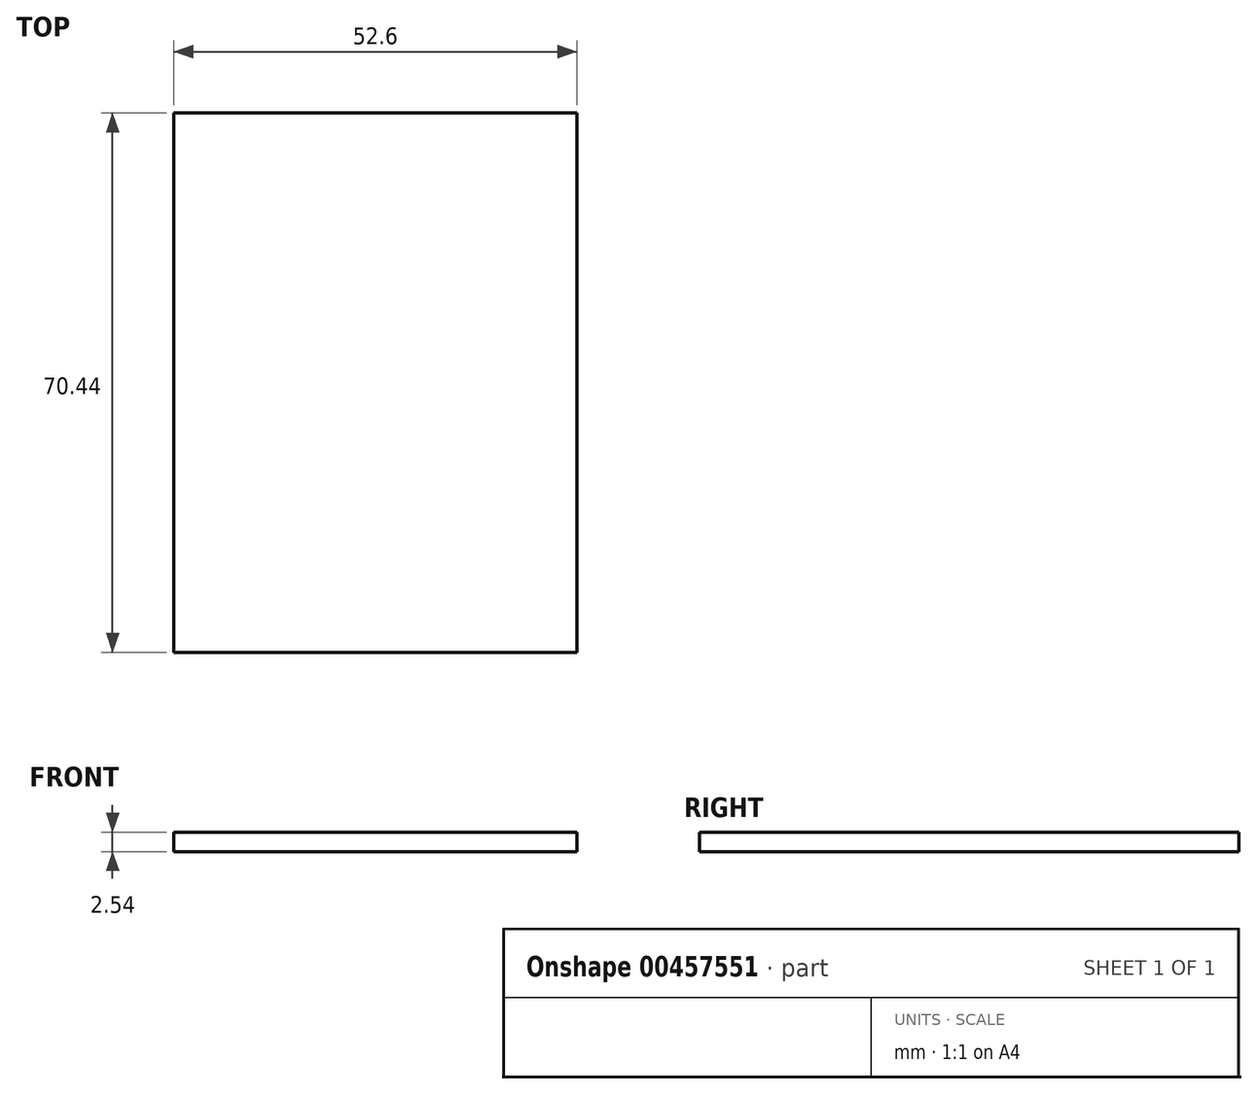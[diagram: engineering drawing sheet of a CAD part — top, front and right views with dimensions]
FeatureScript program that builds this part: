
annotation { "Feature Type Name" : "Feature", "Feature Type Description" : "" }
export const myFeature = defineFeature(function(context is Context, id is Id, definition is map)
    precondition{}
    {
        {
            var Q0;
            Q0=qCreatedBy(makeId("Front.planeOp"),FACE);
            var sketch = newSketch(context, id + "F0", { "sketchPlane" : qUnion([Q0])});
            skCircle(sketch, "E0", {"center": v(0, 0) * mm, "radius": 11.94 * mm});
            skSolve(sketch);
        }
        {
            var Q0;
            Q0=qSketchRegion(id+"F0",true);
            extrude(context, id + "F1", {"entities" : qUnion([Q0]), "depth" : 14.48 * mm});
        }
        {
            var Q0;
            Q0=makeQuery(id+"F1.opExtrude","SWEPT_BODY",BODY,{"disambiguationData":[OSD([sQuery(id+"F0.wireOp",EDGE,"E0")])]});
            deleteBodies(context, id + "F2", {"entities" : qUnion([Q0])});
        }
        {
            var Q0;
            Q0=qCreatedBy(makeId("Front.planeOp"),FACE);
            var sketch = newSketch(context, id + "F3", { "sketchPlane" : qUnion([Q0])});
            skLineSegment(sketch, "E1.bottom", {"start": v(-47.6, 29.63) * mm, "end": v(47.6, 29.63) * mm});
            skLineSegment(sketch, "E1.top", {"start": v(-47.6, -29.63) * mm, "end": v(47.6, -29.63) * mm});
            skLineSegment(sketch, "E1.left", {"start": v(-47.6, 29.63) * mm, "end": v(-47.6, -29.63) * mm});
            skLineSegment(sketch, "E1.right", {"start": v(47.6, 29.63) * mm, "end": v(47.6, -29.63) * mm});
            skPoint(sketch, "E1.middle", {"position": v(0, 0) * mm});
            skSolve(sketch);
        }
        {
            var Q0;
            Q0=makeQuery(id+"F3.imprint","IMPRINT",FACE,{"disambiguationData":[TD([[makeQuery(id+"F3.imprint","IMPRINT",EDGE,{"derivedFrom":sQuery(id+"F3.wireOp",EDGE,"E1.bottom")}),-1.0]])]});
            extrude(context, id + "F4", {"entities" : qUnion([Q0]), "depth" : 25.4 * mm, "hasSecondDirection" : true, "secondDirectionOppositeDirection" : true, "secondDirectionDepth" : 25.4 * mm});
        }
        {
            var Q0;
            Q0=makeQuery(id+"F4.opExtrude","SWEPT_BODY",BODY,{"disambiguationData":[OSD([sQuery(id+"F3.wireOp",EDGE,"E1.bottom"),sQuery(id+"F3.wireOp",EDGE,"E1.top"),sQuery(id+"F3.wireOp",EDGE,"E1.left"),sQuery(id+"F3.wireOp",EDGE,"E1.right")])]});
            deleteBodies(context, id + "F5", {"entities" : qUnion([Q0])});
        }
        {
            var Q0;
            Q0=qCreatedBy(makeId("Top.planeOp"),FACE);
            var sketch = newSketch(context, id + "F6", { "sketchPlane" : qUnion([Q0])});
            skLineSegment(sketch, "E2.bottom", {"start": v(-26.3, 35.22) * mm, "end": v(26.3, 35.22) * mm});
            skLineSegment(sketch, "E2.top", {"start": v(-26.3, -35.22) * mm, "end": v(26.3, -35.22) * mm});
            skLineSegment(sketch, "E2.left", {"start": v(-26.3, 35.22) * mm, "end": v(-26.3, -35.22) * mm});
            skLineSegment(sketch, "E2.right", {"start": v(26.3, 35.22) * mm, "end": v(26.3, -35.22) * mm});
            skPoint(sketch, "E2.middle", {"position": v(0, 0) * mm});
            skSolve(sketch);
        }
        {
            var Q0;
            Q0=makeQuery(id+"F6.imprint","IMPRINT",FACE,{"disambiguationData":[TD([[makeQuery(id+"F6.imprint","IMPRINT",EDGE,{"derivedFrom":sQuery(id+"F6.wireOp",EDGE,"E2.bottom")}),-1.0]])]});
            extrude(context, id + "F7", {"entities" : qUnion([Q0]), "depth" : 2.54 * mm});
        }
    });
